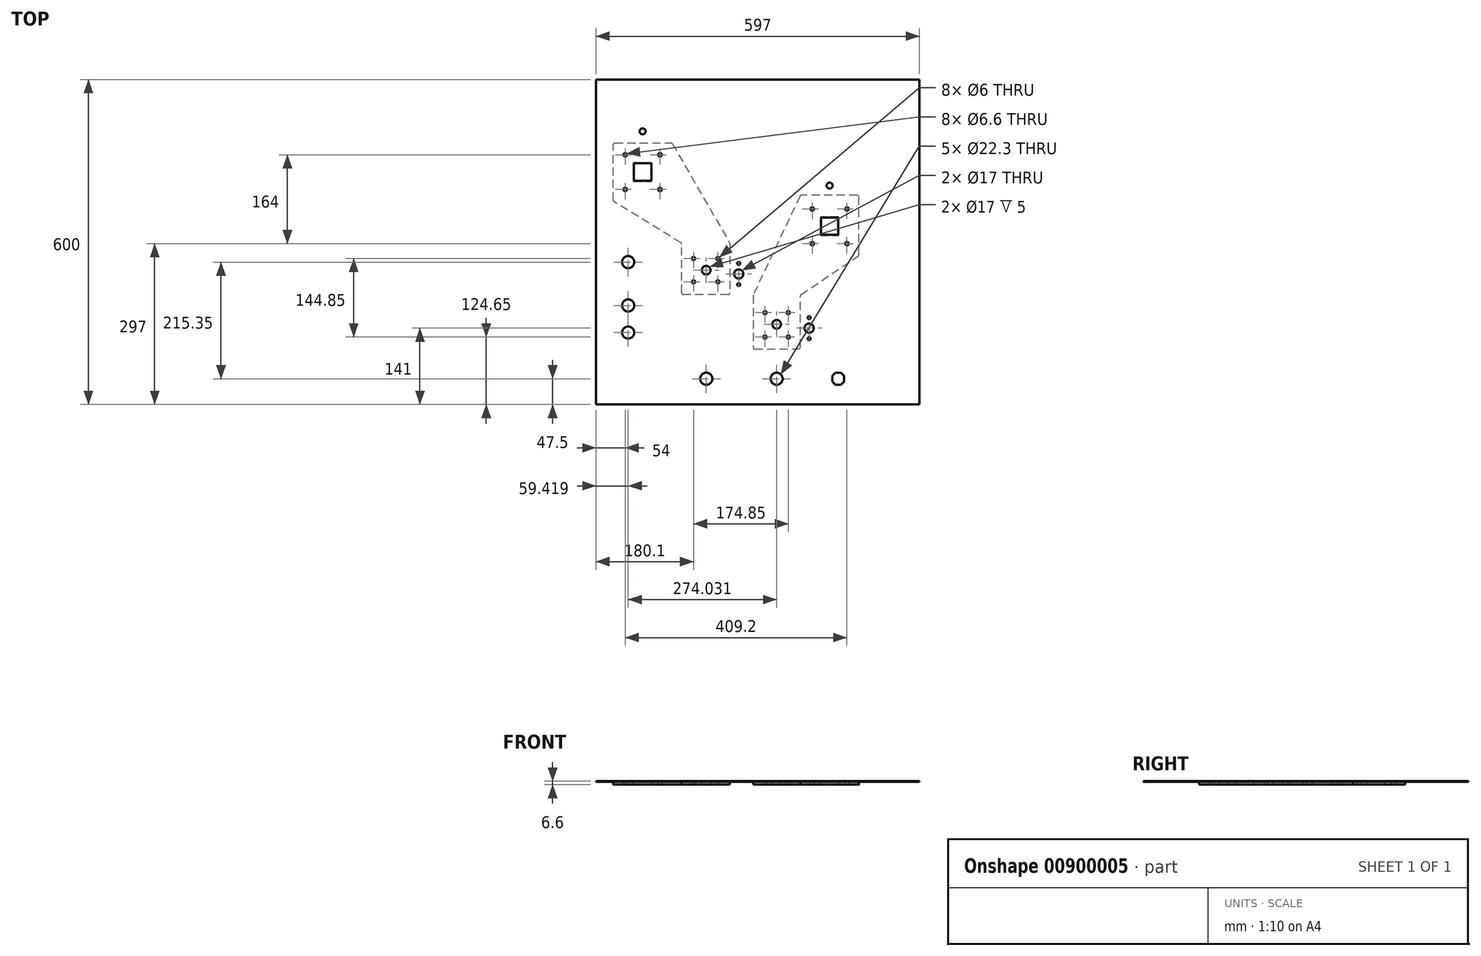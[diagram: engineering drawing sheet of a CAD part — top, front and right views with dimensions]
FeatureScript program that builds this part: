
annotation { "Feature Type Name" : "Feature", "Feature Type Description" : "" }
export const myFeature = defineFeature(function(context is Context, id is Id, definition is map)
    precondition{}
    {
        {
            var Q0;
            Q0=qCreatedBy(makeId("Top.planeOp"),FACE);
            var sketch = newSketch(context, id + "F0", { "sketchPlane" : qUnion([Q0])});
            skLineSegment(sketch, "E0", {"start": v(159.5, -257.76) * mm, "end": v(159.5, -247.24) * mm});
            skLineSegment(sketch, "E1", {"start": v(153.76, -263.5) * mm, "end": v(159.5, -257.76) * mm});
            skLineSegment(sketch, "E2", {"start": v(143.24, -263.5) * mm, "end": v(153.76, -263.5) * mm});
            skLineSegment(sketch, "E3", {"start": v(137.5, -257.76) * mm, "end": v(143.24, -263.5) * mm});
            skLineSegment(sketch, "E4", {"start": v(137.5, -247.24) * mm, "end": v(137.5, -257.76) * mm});
            skLineSegment(sketch, "E5", {"start": v(143.24, -241.5) * mm, "end": v(137.5, -247.24) * mm});
            skLineSegment(sketch, "E6", {"start": v(153.76, -241.5) * mm, "end": v(143.24, -241.5) * mm});
            skLineSegment(sketch, "E7", {"start": v(159.5, -247.24) * mm, "end": v(153.76, -241.5) * mm});
            skCircle(sketch, "E8", {"center": v(132.7, 104.15) * mm, "radius": 5.5 * mm});
            skCircle(sketch, "E9", {"center": v(-212.5, 204.15) * mm, "radius": 5.5 * mm});
            skCircle(sketch, "E10", {"center": v(-239.08, -37.15) * mm, "radius": 11.15 * mm});
            skCircle(sketch, "E11", {"center": v(-239.08, -117.15) * mm, "radius": 11.15 * mm});
            skCircle(sketch, "E12", {"center": v(-239.08, -167.15) * mm, "radius": 11.15 * mm});
            skCircle(sketch, "E13", {"center": v(-95.05, -252.5) * mm, "radius": 11.15 * mm});
            skCircle(sketch, "E14", {"center": v(34.95, -252.5) * mm, "radius": 11.15 * mm});
            skCircle(sketch, "E15", {"center": v(94.95, -139.5) * mm, "radius": 2.75 * mm});
            skCircle(sketch, "E16", {"center": v(94.95, -178.5) * mm, "radius": 2.75 * mm});
            skCircle(sketch, "E17", {"center": v(-35.05, -39.5) * mm, "radius": 2.75 * mm});
            skCircle(sketch, "E18", {"center": v(-35.05, -78.5) * mm, "radius": 2.75 * mm});
            skCircle(sketch, "E19", {"center": v(94.95, -159) * mm, "radius": 8.5 * mm});
            skCircle(sketch, "E20", {"center": v(-35.05, -59) * mm, "radius": 8.5 * mm});
            skCircle(sketch, "E21", {"center": v(34.95, -152) * mm, "radius": 8 * mm});
            skCircle(sketch, "E22", {"center": v(-95.05, -52) * mm, "radius": 8 * mm});
            skCircle(sketch, "E23", {"center": v(56.45, -130.35) * mm, "radius": 3 * mm});
            skCircle(sketch, "E24", {"center": v(13.45, -130.35) * mm, "radius": 3 * mm});
            skCircle(sketch, "E25", {"center": v(56.45, -175.35) * mm, "radius": 3 * mm});
            skCircle(sketch, "E26", {"center": v(13.45, -175.35) * mm, "radius": 3 * mm});
            skCircle(sketch, "E27", {"center": v(-73.4, -30.5) * mm, "radius": 3 * mm});
            skCircle(sketch, "E28", {"center": v(-73.4, -73.5) * mm, "radius": 3 * mm});
            skCircle(sketch, "E29", {"center": v(-118.4, -30.5) * mm, "radius": 3 * mm});
            skCircle(sketch, "E30", {"center": v(-118.4, -73.5) * mm, "radius": 3 * mm});
            skCircle(sketch, "E31", {"center": v(-244.5, 97) * mm, "radius": 3.3 * mm});
            skCircle(sketch, "E32", {"center": v(-244.5, 161) * mm, "radius": 3.3 * mm});
            skCircle(sketch, "E33", {"center": v(-180.5, 97) * mm, "radius": 3.3 * mm});
            skCircle(sketch, "E34", {"center": v(-180.5, 161) * mm, "radius": 3.3 * mm});
            skCircle(sketch, "E35", {"center": v(100.7, 61) * mm, "radius": 3.3 * mm});
            skCircle(sketch, "E36", {"center": v(164.7, 61) * mm, "radius": 3.3 * mm});
            skCircle(sketch, "E37", {"center": v(164.7, -3) * mm, "radius": 3.3 * mm});
            skCircle(sketch, "E38", {"center": v(100.7, -3) * mm, "radius": 3.3 * mm});
            skLineSegment(sketch, "E39", {"start": v(-228.65, 112.85) * mm, "end": v(-196.35, 112.85) * mm});
            skLineSegment(sketch, "E40", {"start": v(-228.65, 145.15) * mm, "end": v(-228.65, 112.85) * mm});
            skLineSegment(sketch, "E41", {"start": v(-196.35, 145.15) * mm, "end": v(-228.65, 145.15) * mm});
            skLineSegment(sketch, "E42", {"start": v(-196.35, 112.85) * mm, "end": v(-196.35, 145.15) * mm});
            skLineSegment(sketch, "E43", {"start": v(148.55, 45.15) * mm, "end": v(116.55, 45.15) * mm});
            skLineSegment(sketch, "E44", {"start": v(148.55, 13.15) * mm, "end": v(148.55, 45.15) * mm});
            skLineSegment(sketch, "E45", {"start": v(116.55, 13.15) * mm, "end": v(148.55, 13.15) * mm});
            skLineSegment(sketch, "E46", {"start": v(116.55, 45.15) * mm, "end": v(116.55, 13.15) * mm});
            skLineSegment(sketch, "E47", {"start": v(-298.5, -300) * mm, "end": v(298.5, -300) * mm});
            skLineSegment(sketch, "E48", {"start": v(298.5, -300) * mm, "end": v(298.5, 300) * mm});
            skLineSegment(sketch, "E49", {"start": v(298.5, 300) * mm, "end": v(-298.5, 300) * mm});
            skLineSegment(sketch, "E50", {"start": v(-298.5, 300) * mm, "end": v(-298.5, -300) * mm});
            skSolve(sketch);
        }
        {
            var Q0;
            Q0=makeQuery(id+"F0.imprint","IMPRINT",FACE,{"disambiguationData":[TD([[makeQuery(id+"F0.imprint","IMPRINT",EDGE,{"derivedFrom":sQuery(id+"F0.wireOp",EDGE,"E0")}),-1.0]])]});
            extrude(context, id + "F1", {"entities" : qUnion([Q0]), "depth" : 1.6 * mm, "offsetDistance" : 25 * mm});
        }
        {
            var Q0;
            Q0=qCreatedBy(makeId("Top.planeOp"),FACE);
            var sketch = newSketch(context, id + "F2", { "sketchPlane" : qUnion([Q0])});
            skCircle(sketch, "E51.0", {"center": v(13.45, -175.35) * mm, "radius": 3 * mm});
            skCircle(sketch, "E52.0", {"center": v(13.45, -130.35) * mm, "radius": 3 * mm});
            skCircle(sketch, "E53.0", {"center": v(34.95, -152) * mm, "radius": 8 * mm});
            skCircle(sketch, "E54.0", {"center": v(56.45, -175.35) * mm, "radius": 3 * mm});
            skCircle(sketch, "E55.0", {"center": v(56.45, -130.35) * mm, "radius": 3 * mm});
            skCircle(sketch, "E56.0", {"center": v(100.7, -3) * mm, "radius": 3.3 * mm});
            skCircle(sketch, "E57.0", {"center": v(164.7, -3) * mm, "radius": 3.3 * mm});
            skCircle(sketch, "E58.0", {"center": v(100.7, 61) * mm, "radius": 3.3 * mm});
            skCircle(sketch, "E59.0", {"center": v(164.7, 61) * mm, "radius": 3.3 * mm});
            skLineSegment(sketch, "E60", {"start": v(78.45, -194.35) * mm, "end": v(78.45, -99.74) * mm});
            skLineSegment(sketch, "E61", {"start": v(79.77, -97.26) * mm, "end": v(185.38, -25.9) * mm});
            skLineSegment(sketch, "E62", {"start": v(186.7, -23.4) * mm, "end": v(186.7, 83.3) * mm});
            skLineSegment(sketch, "E63", {"start": v(183.7, 86.3) * mm, "end": v(80.6, 86.3) * mm});
            skLineSegment(sketch, "E64", {"start": v(77.89, 84.58) * mm, "end": v(-8.26, -97.54) * mm});
            skLineSegment(sketch, "E65", {"start": v(-8.55, -98.82) * mm, "end": v(-8.55, -194.35) * mm});
            skLineSegment(sketch, "E66", {"start": v(-5.55, -197.35) * mm, "end": v(75.45, -197.35) * mm});
            skLineSegment(sketch, "E67.0", {"start": v(116.55, 45.15) * mm, "end": v(116.55, 13.15) * mm, "construction": true});
            skLineSegment(sketch, "E68.0", {"start": v(116.55, 13.15) * mm, "end": v(148.55, 13.15) * mm, "construction": true});
            skLineSegment(sketch, "E69.0", {"start": v(148.55, 13.15) * mm, "end": v(148.55, 45.15) * mm, "construction": true});
            skLineSegment(sketch, "E70.0", {"start": v(148.55, 45.15) * mm, "end": v(116.55, 45.15) * mm, "construction": true});
            skPoint(sketch, "E71.visualSharp", {"position": v(-8.55, -98.15) * mm});
            skArc(sketch, "E71.filletArc", {"start": v(-8.26, -97.54) * mm, "mid": v(-8.48, -98.17) * mm, "end": v(-8.55, -98.82) * mm});
            skPoint(sketch, "E72.visualSharp", {"position": v(-8.55, -197.35) * mm});
            skArc(sketch, "E72.filletArc", {"start": v(-8.55, -194.35) * mm, "mid": v(-7.67, -196.47) * mm, "end": v(-5.55, -197.35) * mm});
            skPoint(sketch, "E73.visualSharp", {"position": v(78.45, -197.35) * mm});
            skArc(sketch, "E73.filletArc", {"start": v(75.45, -197.35) * mm, "mid": v(77.57, -196.47) * mm, "end": v(78.45, -194.35) * mm});
            skPoint(sketch, "E74.visualSharp", {"position": v(78.45, -98.15) * mm});
            skArc(sketch, "E74.filletArc", {"start": v(79.77, -97.26) * mm, "mid": v(78.8, -98.34) * mm, "end": v(78.45, -99.74) * mm});
            skPoint(sketch, "E75.visualSharp", {"position": v(186.7, -25) * mm});
            skArc(sketch, "E75.filletArc", {"start": v(185.38, -25.9) * mm, "mid": v(186.35, -24.81) * mm, "end": v(186.7, -23.4) * mm});
            skPoint(sketch, "E76.visualSharp", {"position": v(186.7, 86.3) * mm});
            skArc(sketch, "E76.filletArc", {"start": v(186.7, 83.3) * mm, "mid": v(185.82, 85.42) * mm, "end": v(183.7, 86.3) * mm});
            skPoint(sketch, "E77.visualSharp", {"position": v(78.7, 86.3) * mm});
            skArc(sketch, "E77.filletArc", {"start": v(80.6, 86.3) * mm, "mid": v(79, 85.83) * mm, "end": v(77.89, 84.58) * mm});
            skLineSegment(sketch, "E78.0", {"start": v(149.55, 46.15) * mm, "end": v(115.55, 46.15) * mm});
            skLineSegment(sketch, "E78.1", {"start": v(149.55, 12.15) * mm, "end": v(149.55, 46.15) * mm});
            skLineSegment(sketch, "E78.2", {"start": v(115.55, 12.15) * mm, "end": v(149.55, 12.15) * mm});
            skLineSegment(sketch, "E78.3", {"start": v(115.55, 46.15) * mm, "end": v(115.55, 12.15) * mm});
            skLineSegment(sketch, "E79.0", {"start": v(-303.5, 305) * mm, "end": v(303.5, 305) * mm, "construction": true});
            skLineSegment(sketch, "E79.1", {"start": v(-303.5, -305) * mm, "end": v(-303.5, 305) * mm, "construction": true});
            skLineSegment(sketch, "E79.2", {"start": v(303.5, -305) * mm, "end": v(-303.5, -305) * mm, "construction": true});
            skLineSegment(sketch, "E79.3", {"start": v(303.5, 305) * mm, "end": v(303.5, -305) * mm, "construction": true});
            skCircle(sketch, "E80", {"center": v(34.95, -152) * mm, "radius": 8.5 * mm});
            skSolve(sketch);
        }
        {
            var Q0;
            Q0 = qSketchRegion(id + "F2", true);
            extrude(context, id + "F3", {"entities" : qUnion([Q0]), "operationType" : NewBodyOperationType.ADD, "oppositeDirection" : true, "depth" : 5 * mm, "offsetDistance" : 25 * mm});
        }
        {
            var Q0;
            Q0=makeQuery(id+"F1.opExtrude","CAP_FACE",FACE,{"disambiguationData":[OSD([sQuery(id+"F0.wireOp",EDGE,"E0"),sQuery(id+"F0.wireOp",EDGE,"E1"),sQuery(id+"F0.wireOp",EDGE,"E2"),sQuery(id+"F0.wireOp",EDGE,"E3"),sQuery(id+"F0.wireOp",EDGE,"E4"),sQuery(id+"F0.wireOp",EDGE,"E5"),sQuery(id+"F0.wireOp",EDGE,"E6"),sQuery(id+"F0.wireOp",EDGE,"E7"),sQuery(id+"F0.wireOp",EDGE,"E8"),sQuery(id+"F0.wireOp",EDGE,"E9"),sQuery(id+"F0.wireOp",EDGE,"E10"),sQuery(id+"F0.wireOp",EDGE,"E11"),sQuery(id+"F0.wireOp",EDGE,"E12"),sQuery(id+"F0.wireOp",EDGE,"E13"),sQuery(id+"F0.wireOp",EDGE,"E14"),sQuery(id+"F0.wireOp",EDGE,"E15"),sQuery(id+"F0.wireOp",EDGE,"E16"),sQuery(id+"F0.wireOp",EDGE,"E17"),sQuery(id+"F0.wireOp",EDGE,"E18"),sQuery(id+"F0.wireOp",EDGE,"E19"),sQuery(id+"F0.wireOp",EDGE,"E20"),sQuery(id+"F0.wireOp",EDGE,"E21"),sQuery(id+"F0.wireOp",EDGE,"E22"),sQuery(id+"F0.wireOp",EDGE,"E23"),sQuery(id+"F0.wireOp",EDGE,"E24"),sQuery(id+"F0.wireOp",EDGE,"E25"),sQuery(id+"F0.wireOp",EDGE,"E26"),sQuery(id+"F0.wireOp",EDGE,"E27"),sQuery(id+"F0.wireOp",EDGE,"E28"),sQuery(id+"F0.wireOp",EDGE,"E29"),sQuery(id+"F0.wireOp",EDGE,"E30"),sQuery(id+"F0.wireOp",EDGE,"E31"),sQuery(id+"F0.wireOp",EDGE,"E32"),sQuery(id+"F0.wireOp",EDGE,"E33"),sQuery(id+"F0.wireOp",EDGE,"E34"),sQuery(id+"F0.wireOp",EDGE,"E35"),sQuery(id+"F0.wireOp",EDGE,"E36"),sQuery(id+"F0.wireOp",EDGE,"E37"),sQuery(id+"F0.wireOp",EDGE,"E38"),sQuery(id+"F0.wireOp",EDGE,"E39"),sQuery(id+"F0.wireOp",EDGE,"E40"),sQuery(id+"F0.wireOp",EDGE,"E41"),sQuery(id+"F0.wireOp",EDGE,"E42"),sQuery(id+"F0.wireOp",EDGE,"E43"),sQuery(id+"F0.wireOp",EDGE,"E44"),sQuery(id+"F0.wireOp",EDGE,"E45"),sQuery(id+"F0.wireOp",EDGE,"E46"),sQuery(id+"F0.wireOp",EDGE,"E47"),sQuery(id+"F0.wireOp",EDGE,"E48"),sQuery(id+"F0.wireOp",EDGE,"E49"),sQuery(id+"F0.wireOp",EDGE,"E50")])],"isStart":true});
            var sketch = newSketch(context, id + "F4", { "sketchPlane" : qUnion([Q0])});
            skLineSegment(sketch, "E81", {"start": v(-140.4, 93.98) * mm, "end": v(-140.4, 3.76) * mm});
            skLineSegment(sketch, "E82", {"start": v(-141.84, 1.2) * mm, "end": v(-265.06, -74.12) * mm});
            skLineSegment(sketch, "E83", {"start": v(-266.5, -76.68) * mm, "end": v(-266.5, -180) * mm});
            skLineSegment(sketch, "E84", {"start": v(-263.5, -183) * mm, "end": v(-160.23, -183) * mm});
            skLineSegment(sketch, "E85", {"start": v(-157.63, -181.5) * mm, "end": v(-51.8, 1.38) * mm});
            skLineSegment(sketch, "E86", {"start": v(-51.4, 2.89) * mm, "end": v(-51.4, 93.98) * mm});
            skLineSegment(sketch, "E87", {"start": v(-54.4, 96.98) * mm, "end": v(-137.4, 96.98) * mm});
            skCircle(sketch, "E88.0", {"center": v(-118.4, 73.5) * mm, "radius": 3 * mm});
            skCircle(sketch, "E89.0", {"center": v(-73.4, 73.5) * mm, "radius": 3 * mm});
            skCircle(sketch, "E90.0", {"center": v(-95.05, 52) * mm, "radius": 8 * mm, "construction": true});
            skCircle(sketch, "E91.0", {"center": v(-118.4, 30.5) * mm, "radius": 3 * mm});
            skCircle(sketch, "E92.0", {"center": v(-73.4, 30.5) * mm, "radius": 3 * mm});
            skCircle(sketch, "E93.0", {"center": v(-244.5, -97) * mm, "radius": 3.3 * mm});
            skCircle(sketch, "E94.0", {"center": v(-180.5, -97) * mm, "radius": 3.3 * mm});
            skCircle(sketch, "E95.0", {"center": v(-180.5, -161) * mm, "radius": 3.3 * mm});
            skCircle(sketch, "E96.0", {"center": v(-244.5, -161) * mm, "radius": 3.3 * mm});
            skLineSegment(sketch, "E97.0", {"start": v(-228.65, -112.85) * mm, "end": v(-196.35, -112.85) * mm, "construction": true});
            skLineSegment(sketch, "E98.0", {"start": v(-228.65, -145.15) * mm, "end": v(-228.65, -112.85) * mm, "construction": true});
            skLineSegment(sketch, "E99.0", {"start": v(-196.35, -145.15) * mm, "end": v(-228.65, -145.15) * mm, "construction": true});
            skLineSegment(sketch, "E100.0", {"start": v(-196.35, -112.85) * mm, "end": v(-196.35, -145.15) * mm, "construction": true});
            skPoint(sketch, "E101.visualSharp", {"position": v(-140.4, 96.98) * mm});
            skArc(sketch, "E101.filletArc", {"start": v(-137.4, 96.98) * mm, "mid": v(-139.52, 96.1) * mm, "end": v(-140.4, 93.98) * mm});
            skPoint(sketch, "E102.visualSharp", {"position": v(-51.4, 96.98) * mm});
            skArc(sketch, "E102.filletArc", {"start": v(-51.4, 93.98) * mm, "mid": v(-52.28, 96.1) * mm, "end": v(-54.4, 96.98) * mm});
            skPoint(sketch, "E103.visualSharp", {"position": v(-51.4, 2.08) * mm});
            skArc(sketch, "E103.filletArc", {"start": v(-51.8, 1.38) * mm, "mid": v(-51.5, 2.1) * mm, "end": v(-51.4, 2.89) * mm});
            skPoint(sketch, "E104.visualSharp", {"position": v(-158.5, -183) * mm});
            skArc(sketch, "E104.filletArc", {"start": v(-160.23, -183) * mm, "mid": v(-158.73, -182.6) * mm, "end": v(-157.63, -181.5) * mm});
            skPoint(sketch, "E105.visualSharp", {"position": v(-266.5, -183) * mm});
            skArc(sketch, "E105.filletArc", {"start": v(-266.5, -180) * mm, "mid": v(-265.62, -182.12) * mm, "end": v(-263.5, -183) * mm});
            skPoint(sketch, "E106.visualSharp", {"position": v(-266.5, -75) * mm});
            skArc(sketch, "E106.filletArc", {"start": v(-265.06, -74.12) * mm, "mid": v(-266.12, -75.21) * mm, "end": v(-266.5, -76.68) * mm});
            skPoint(sketch, "E107.visualSharp", {"position": v(-140.4, 2.08) * mm});
            skArc(sketch, "E107.filletArc", {"start": v(-141.84, 1.2) * mm, "mid": v(-140.78, 2.3) * mm, "end": v(-140.4, 3.76) * mm});
            skCircle(sketch, "E108", {"center": v(-95.05, 52) * mm, "radius": 8.5 * mm});
            skLineSegment(sketch, "E109.0", {"start": v(-229.65, -111.85) * mm, "end": v(-195.35, -111.85) * mm});
            skLineSegment(sketch, "E109.1", {"start": v(-229.65, -146.15) * mm, "end": v(-229.65, -111.85) * mm});
            skLineSegment(sketch, "E109.2", {"start": v(-195.35, -146.15) * mm, "end": v(-229.65, -146.15) * mm});
            skLineSegment(sketch, "E109.3", {"start": v(-195.35, -111.85) * mm, "end": v(-195.35, -146.15) * mm});
            skSolve(sketch);
        }
        {
            var Q0;
            Q0 = qSketchRegion(id + "F4", true);
            extrude(context, id + "F5", {"entities" : qUnion([Q0]), "operationType" : NewBodyOperationType.ADD, "depth" : 5 * mm, "offsetDistance" : 25 * mm});
        }
    });
